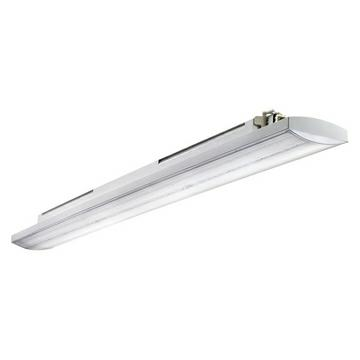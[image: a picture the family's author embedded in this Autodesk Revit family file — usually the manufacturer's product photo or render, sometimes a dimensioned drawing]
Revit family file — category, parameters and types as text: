
# Revit family: Lighting-Industrial-GEWISS-SMART[3]PLUS-HLO-WATERTIGHT-LED_TRANSPARENT_1600mm
name_source: partatom
category: Apparecchi per illuminazione
units: mm (PartAtom-declared; Revit-internal decimal feet)

## family parameters
Condiviso = No
Host = Superficie
Punto di calcolo locali = No
Quota connettore circolare = Usa diametro
Sorgente d'illuminazione = Sì
Taglio con vuoti quando caricato = No
Tipo di parte = Normale

## types (1)
- Lighting-Industrial-GEWISS-SMART[3]PLUS-HLO-WATERTIGHT-LED_TRANSPARENT_1600mm
    Angolo inclinazione = -90.00°
    Application = Indoor
    Carico apparente = 67 VA
    Catalogue = LIGHTING
    Catalogue Range = SMART[3] PLUS HLO
    Colour temperature = 5700 K (CRI > 90)
    Colour temperature: = 5700 K (CRI > 90)
    Commenti sul wattaggio = 67W
    Descrizione = SMART3 PLUS 1600 T.W.DALI HO TRASP 9 57
    Efficiency class of integrated LEDs = A ÷ A++
    Electrocod = 2434
    Emetti da lunghezza linea = 1200 mm
    File diagramma fotometrico = GWS3323BT957.IES
    Filtro dei colori = 16777215
    Ganci = Alluminio
    Glow Wire Test = 850°C
    IDF = 9980e4de-da63-47da-a8b3-d302d63a2e3d
    IDT = a13ebeb2-bfa1-469e-9c7f-0ca841da0dbd
    IP degree = IP66/IP69
    Immagine tipo = GWS3280TS.jpg
    Insulation class = II
    Lamp = LED
    Lampada = LED
    Length = 1600 mm
    Lumen output (lm) = 7400
    Lunghezza Lampada = 1600 mm  [stored 5.24934 ft]
    Modello = GWS3323BT957
    Numero poli = 2
    Operating temperature: = -25 +45 °C
    Produttore = GEWISS S.p.A.
    Prospetto di default = 1219 mm
    SEO = Ceiling
    Schermo. = Led Acceso
    Shield type = Transparent
    Shock resistance = IK08
    Stampa 1_100 = Sì
    Stampa 1_200 = No
    Struttura = GRIGIO
    System power = 63 W
    Technical sheet = https://www.gewiss.com
    Type of light source = LED - Not replaceable
    Typology = DALI
    URL = https://www.gewiss.com
    Variazione temperatura colore lampada con luminosità attenuata = <Nessuno>
    Version file RFA = 20.0
    Voltage = 220-240 V
    Warranty = 5 years
    Working temperature = -25 +45 °C

note: [stored X ft] marks values corroborated as IEEE doubles in the binary element streams (Revit-internal decimal feet)
